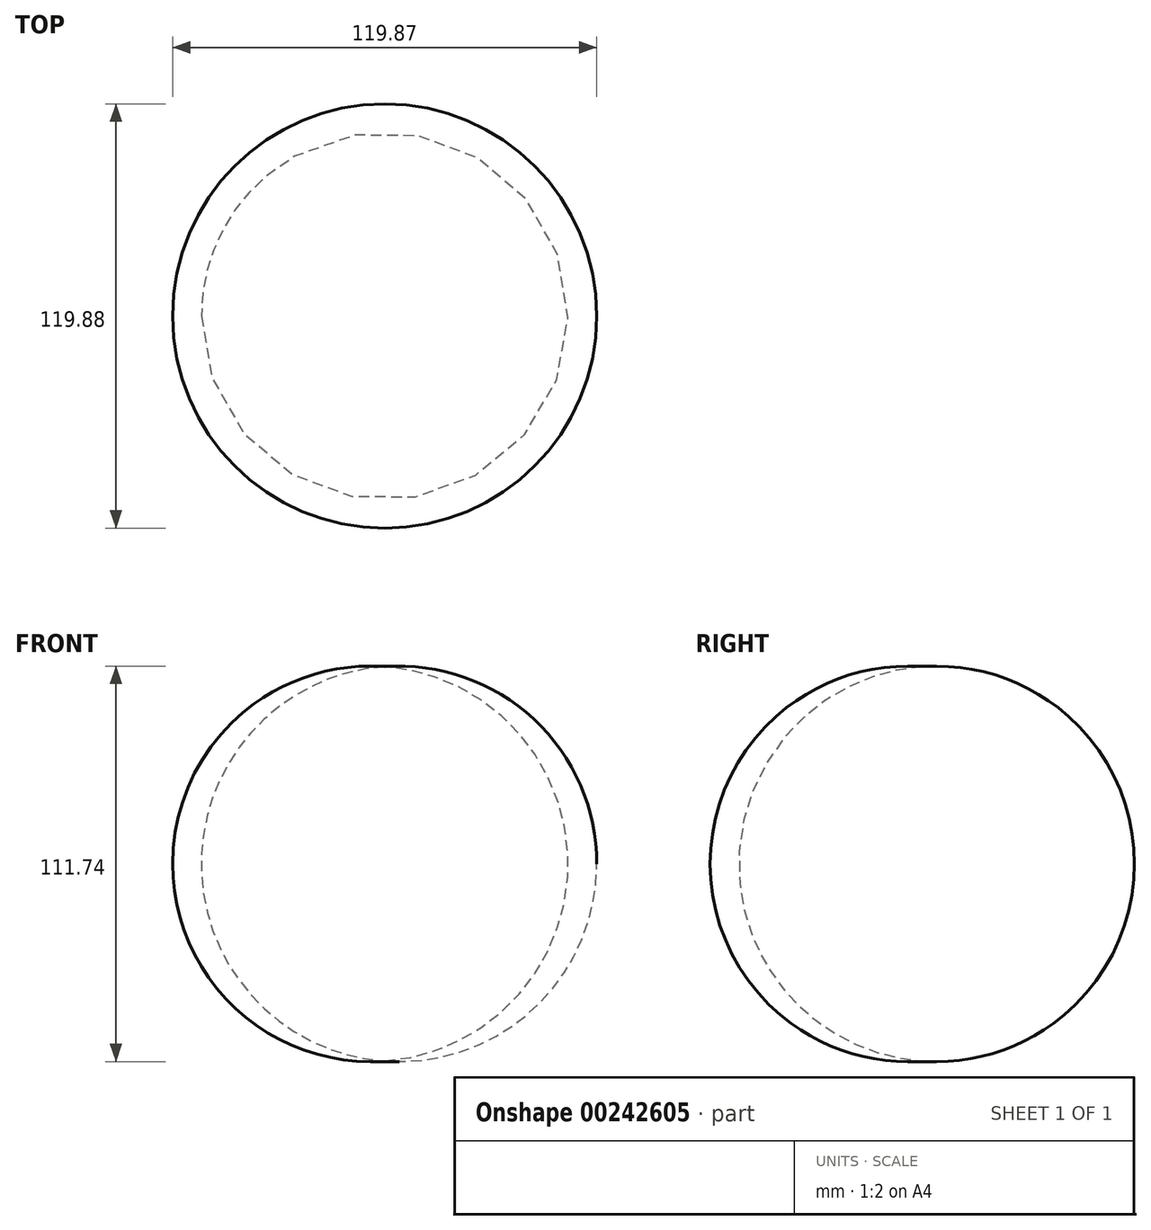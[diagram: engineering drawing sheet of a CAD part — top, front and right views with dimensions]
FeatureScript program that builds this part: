
annotation { "Feature Type Name" : "Feature", "Feature Type Description" : "" }
export const myFeature = defineFeature(function(context is Context, id is Id, definition is map)
    precondition{}
    {
        {
            var Q0;
            Q0=qCreatedBy(makeId("Front.planeOp"),FACE);
            var sketch = newSketch(context, id + "F0", { "sketchPlane" : qUnion([Q0])});
            skLineSegment(sketch, "E0", {"start": v(-33.67, 55.57) * mm, "end": v(-33.67, -55.87) * mm});
            skArc(sketch, "E1", {"start": v(-33.67, -55.87) * mm, "mid": v(18.13, -0.15) * mm, "end": v(-33.67, 55.57) * mm});
            skSolve(sketch);
        }
        {
            var Q0;
            Q0=makeQuery(id+"F0.imprint","IMPRINT",FACE,{"disambiguationData":[TD([[makeQuery(id+"F0.imprint","IMPRINT",EDGE,{"derivedFrom":sQuery(id+"F0.wireOp",EDGE,"E0")}),1.0]])]});
            var Q1;
            Q1=sQuery(id+"F0.wireOp",EDGE,"E0");
            revolve(context, id + "F1", {"entities" : qUnion([Q0]), "axis" : qUnion([Q1]), "revolveType" : RevolveType.FULL});
        }
    });
